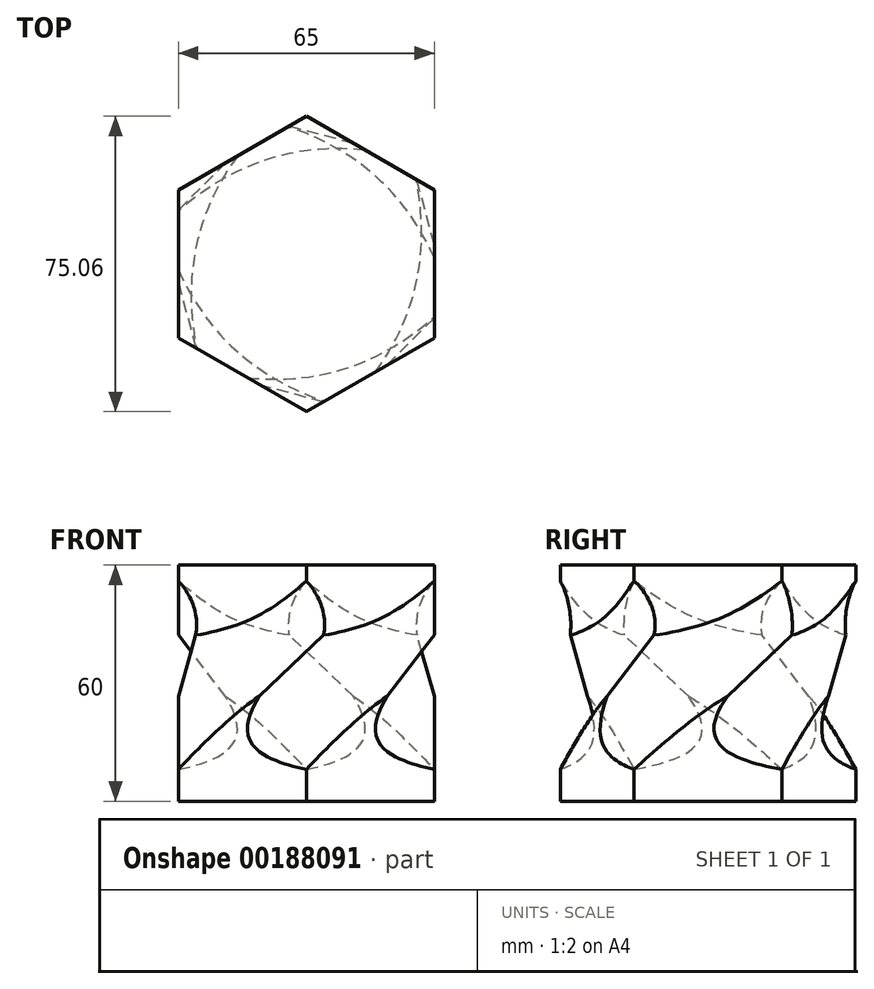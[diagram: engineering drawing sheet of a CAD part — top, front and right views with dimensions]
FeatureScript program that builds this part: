
annotation { "Feature Type Name" : "Feature", "Feature Type Description" : "" }
export const myFeature = defineFeature(function(context is Context, id is Id, definition is map)
    precondition{}
    {
        {
            var Q0;
            Q0=qCreatedBy(makeId("Top.planeOp"),FACE);
            var sketch = newSketch(context, id + "F0", { "sketchPlane" : qUnion([Q0])});
            skCircle(sketch, "E0.cCircle", {"center": v(0, 0) * mm, "radius": 40 * mm, "construction": true});
            skLineSegment(sketch, "E0.0", {"start": v(0, 46.19) * mm, "end": v(40, 23.1) * mm});
            skLineSegment(sketch, "E0.1", {"start": v(40, 23.1) * mm, "end": v(40, -23.1) * mm});
            skLineSegment(sketch, "E0.2", {"start": v(40, -23.1) * mm, "end": v(0, -46.19) * mm});
            skLineSegment(sketch, "E0.3", {"start": v(0, -46.19) * mm, "end": v(-40, -23.1) * mm});
            skLineSegment(sketch, "E0.4", {"start": v(-40, -23.1) * mm, "end": v(-40, 23.1) * mm});
            skLineSegment(sketch, "E0.5", {"start": v(-40, 23.1) * mm, "end": v(0, 46.19) * mm});
            skPoint(sketch, "E0.0.midPoint", {"position": v(20, 34.64) * mm});
            skSolve(sketch);
        }
        {
            var Q0;
            Q0=makeQuery(id+"F0.imprint","IMPRINT",FACE,{"disambiguationData":[TD([[makeQuery(id+"F0.imprint","IMPRINT",EDGE,{"derivedFrom":sQuery(id+"F0.wireOp",EDGE,"E0.0")}),-1.0]])]});
            cPlane(context, id + "F1", {"entities" : qUnion([Q0]), "cplaneType" : CPlaneType.OFFSET, "offset" : 60 * mm, "width" : 150 * mm, "height" : 150 * mm});
        }
        {
            var Q0;
            Q0=qCreatedBy(id+"F1.planeOp",FACE);
            var sketch = newSketch(context, id + "F2", { "sketchPlane" : qUnion([Q0])});
            skCircle(sketch, "E1.cCircle", {"center": v(0, 0) * mm, "radius": 40 * mm, "construction": true});
            skLineSegment(sketch, "E1.0", {"start": v(23.1, 40) * mm, "end": v(46.19, 0) * mm});
            skLineSegment(sketch, "E1.1", {"start": v(46.19, 0) * mm, "end": v(23.1, -40) * mm});
            skLineSegment(sketch, "E1.2", {"start": v(23.1, -40) * mm, "end": v(-23.1, -40) * mm});
            skLineSegment(sketch, "E1.3", {"start": v(-23.1, -40) * mm, "end": v(-46.19, 0) * mm});
            skLineSegment(sketch, "E1.4", {"start": v(-46.19, 0) * mm, "end": v(-23.1, 40) * mm});
            skLineSegment(sketch, "E1.5", {"start": v(-23.1, 40) * mm, "end": v(23.1, 40) * mm});
            skPoint(sketch, "E1.0.midPoint", {"position": v(34.64, 20) * mm});
            skSolve(sketch);
        }
        {
            var Q0;
            Q0=sQuery(id+"F0.wireOp",VERTEX,"E0.4.start");
            var Q1;
            Q1=sQuery(id+"F2.wireOp",VERTEX,"E1.2.start");
            var Q2;
            Q2=sQuery(id+"F0.wireOp",VERTEX,"E0.3.start");
            cPlane(context, id + "F3", {"entities" : qUnion([Q0, Q1, Q2]), "cplaneType" : CPlaneType.THREE_POINT, "offset" : 25 * mm, "width" : 150 * mm, "height" : 150 * mm});
        }
        {
            var Q0;
            Q0=qCreatedBy(id+"F3.planeOp",FACE);
            var sketch = newSketch(context, id + "F4", { "sketchPlane" : qUnion([Q0])});
            skLineSegment(sketch, "E2", {"start": v(21.14, -14.3) * mm, "end": v(-24.5, -7.15) * mm});
            skLineSegment(sketch, "E3", {"start": v(47.48, 44.68) * mm, "end": v(-31.55, 57.06) * mm});
            skLineSegment(sketch, "E4", {"start": v(-24.5, -7.15) * mm, "end": v(47.48, 44.68) * mm});
            skSolve(sketch);
        }
        {
            var Q0;
            Q0=makeQuery(id+"F0.imprint","IMPRINT",FACE,{"disambiguationData":[TD([[makeQuery(id+"F0.imprint","IMPRINT",EDGE,{"derivedFrom":sQuery(id+"F0.wireOp",EDGE,"E0.0")}),-1.0]])]});
            var Q1;
            Q1=makeQuery(id+"F2.imprint","IMPRINT",FACE,{"disambiguationData":[TD([[makeQuery(id+"F2.imprint","IMPRINT",EDGE,{"derivedFrom":sQuery(id+"F2.wireOp",EDGE,"E1.0")}),-1.0]])]});
            var Q2;
            Q2=sQuery(id+"F4.wireOp",EDGE,"E4");
            loft(context, id + "F5", {"addGuides" : true, "sheetProfilesArray" : [{ "sheetProfileEntities" : qUnion([Q0]) }, { "sheetProfileEntities" : qUnion([Q1]) }], "guidesArray" : [{ "guideEntities" : qUnion([Q2]), "guideDerivativeType" : LoftGuideDerivativeType.DEFAULT, "guideDerivativeMagnitude" : 1 }]});
        }
        {
            var Q0;
            Q0=makeQuery(id+"F5.opLoft","CAP_FACE",FACE,{"disambiguationData":[OSD([makeQuery(id+"F2.imprint","IMPRINT",FACE,{"disambiguationData":[TD([[makeQuery(id+"F2.imprint","IMPRINT",EDGE,{"derivedFrom":sQuery(id+"F2.wireOp",EDGE,"E1.0")}),-1.0]])]})])],"isStart":true});
            var sketch = newSketch(context, id + "F6", { "sketchPlane" : qUnion([Q0])});
            skLineSegment(sketch, "E5", {"start": v(-46.19, 0) * mm, "end": v(0, 0) * mm});
            skLineSegment(sketch, "E6", {"start": v(0, 0) * mm, "end": v(-23.1, 40) * mm});
            skLineSegment(sketch, "E7", {"start": v(0, 0) * mm, "end": v(23.1, 40) * mm});
            skCircle(sketch, "E8.cCircle", {"center": v(0, 0) * mm, "radius": 32.5 * mm, "construction": true});
            skLineSegment(sketch, "E8.0", {"start": v(-32.5, 18.76) * mm, "end": v(0, 37.53) * mm});
            skLineSegment(sketch, "E8.1", {"start": v(0, 37.53) * mm, "end": v(32.5, 18.76) * mm});
            skLineSegment(sketch, "E8.2", {"start": v(32.5, 18.76) * mm, "end": v(32.5, -18.76) * mm});
            skLineSegment(sketch, "E8.3", {"start": v(32.5, -18.76) * mm, "end": v(0, -37.53) * mm});
            skLineSegment(sketch, "E8.4", {"start": v(0, -37.53) * mm, "end": v(-32.5, -18.76) * mm});
            skLineSegment(sketch, "E8.5", {"start": v(-32.5, -18.76) * mm, "end": v(-32.5, 18.76) * mm});
            skPoint(sketch, "E8.0.midPoint", {"position": v(-16.25, 28.15) * mm});
            skSolve(sketch);
        }
        {
            var Q0;
            Q0 = qSketchRegion(id + "F6", true);
            extrude(context, id + "F7", {"entities" : qUnion([Q0]), "operationType" : NewBodyOperationType.INTERSECT, "endBound" : BoundingType.THROUGH_ALL, "oppositeDirection" : true, "depth" : 25 * mm});
        }
    });
